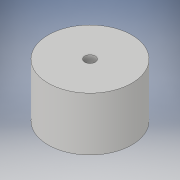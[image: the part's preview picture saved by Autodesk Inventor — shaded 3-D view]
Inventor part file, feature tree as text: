
AUTODESK INVENTOR PART (.ipt)
format: ipt  version: 2019 (Build 230136000, 136)  size: 96,256 bytes
history: native  units: mm
features: thicken_offset x2, extrude x1, sketch x1
ambient origin geometry x8: Origin, YZ Plane, XZ Plane, XY Plane, X Axis, Y Axis, Z Axis, Center Point
bodies: Solid1 (feature_tree)
feature tree (4):
  extrude  "Extrusion1"  Depth=25.0mm
  thicken_offset  "Thicken1"
  thicken_offset  "Thicken2"
  sketch  "Sketch1"  dims[d0=35.0mm d1=5.0mm d2=25.0mm d3=0.0mm d4=1.0mm d5=1.0mm d6=1.0mm d7=1.0mm]
